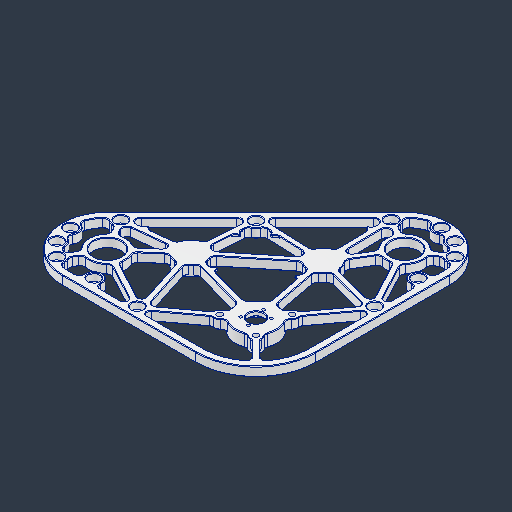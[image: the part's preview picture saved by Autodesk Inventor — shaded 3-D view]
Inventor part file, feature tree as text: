
AUTODESK INVENTOR PART (.ipt)
format: ipt  version: 2024.3 (Build 283343000, 343)  size: 854,016 bytes
history: native  units: in
note: dims shown in document units (in); Inventor stores cm internally (conversion verified against a paired STEP export)
features: chamfer x1
ambient origin geometry x8: Origin, YZ Plane, XZ Plane, XY Plane, X Axis, Y Axis, Z Axis, Center Point
bodies: Solid14 (feature_tree)
feature tree (1):
  chamfer  "Chamfer1"  [1 undecoded]
note: 1 required parameter value undecoded (feature->parameter linkage not recoverable at this tier; creation-order binding heuristic only, values carry confidence <= 0.55)
